# Revit family: Haworth_ImprovSide_Chair_LegBase
name_source: partatom
category: Furniture
revit_build: Autodesk Revit 2018 (Build: 20170223_1515(x64)
units: mm (PartAtom-declared; Revit-internal decimal feet)

## family parameters
Always vertical = Yes
Cut with Voids When Loaded = No
OmniClass Number = 23.40.20.00
OmniClass Title = General Furniture and Specialties
Room Calculation Point = No
Shared = No
Work Plane-Based = No

## types (2) — shared parameters
Actual Depth = 1' - 10 11/16"
Actual Height = 2' - 8"
Actual Width = 1' - 8 13/16"
Arm Cap Finish = Haworth _ Polymer _ Fog
Assembly Code = E2020200
Caster Void = 1' - 10"
Casters = Yes
Depth = 21.5 in.
Description = Haworth - Chair - Improv - Side - Stacking
Frame Finish = Haworth _ Paint _ Graphite
Front Leg Height = 1' - 11 1/2"
Front Void Offset = -0' - 0 1/4"
Glides = No
Height = 32 in.
Manufacturer = Haworth
Model = Haworth - Chair - Improv - Side - Stacking
Revision = 4
Seat Finish = Haworth _ Fabric _ Tellure _ Tomato 3A-43
Size = Verify Final Dim. w/ Haworth
Sustainability Info = http://www.haworth.com
URL = http://haworth.com
URL - Product = http://www.haworth.com
Warranty = http://www.haworth.com
Width = 22 in.
With Arms = Yes
Without Arms = No

## per-type parameters (varying)
| type | Back Finish | Wood Back |
| Upholstered Back | Haworth _ Fabric _ Tellure _ Tomato 3A-43 | No |
| Wood Back | Haworth _ Wood _ White Oak | Yes |

type visibility flags (boolean, named after types; folded from table):
- Upholstered Back: Yes: Upholstered Back
- Wood Back: Yes: (none)

## geometry (parser evidence)
native form markers: Sweep x5
no freeform markers — native parametric forms only
